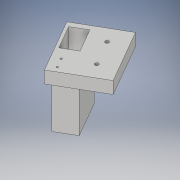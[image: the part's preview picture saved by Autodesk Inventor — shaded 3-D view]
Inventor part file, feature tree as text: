
AUTODESK INVENTOR PART (.ipt)
format: ipt  version: 2017 (Build 210142000, 142)  size: 245,248 bytes
history: native  units: in
note: dims shown in document units (in); Inventor stores cm internally (conversion verified against a paired STEP export)
features: extrude x7, sketch x7, projected_geometry x7, imported_body x1
ambient origin geometry x8: Origin, YZ Plane, XZ Plane, XY Plane, X Axis, Y Axis, Z Axis, Center Point
bodies: Solid1 (feature_tree)
feature tree (22):
  extrude  "Extrusion1"  Depth=0.3937in TaperAngle=0.0deg
  extrude  "Extrusion2"  Depth=0.3937in TaperAngle=0.0deg
  extrude  "Extrusion4"  Depth=0.3937in TaperAngle=0.0deg
  extrude  "Extrusion5"  Depth=0.3937in TaperAngle=0.0deg
  extrude  "Extrusion6"  Depth=0.188in
  extrude  "limit switch"  Depth=0.125in
  extrude  "Extrusion8"  Depth=0.3937in
  sketch  "Sketch1"  dims[d0=1.25in d1=0.3937in d2=0.0in]
  projected_geometry  "Projected Loop1"
  sketch  "Sketch2"  dims[d3=0.125in d4=0.3937in d5=0.0in]
  sketch  "Sketch4"  dims[d9=0.4331in d10=0.3937in d11=0.0in]
  projected_geometry  "Projected Loop3"
  sketch  "Sketch5"  dims[d12=0.3937in d13=0.3937in d14=0.0in]
  projected_geometry  "Projected Loop4"
  sketch  "Sketch6"  dims[d15=0.765in d16=0.188in]
  projected_geometry  "Projected Loop5"
  sketch  "Sketch7"  dims[d17=0.5in d18=0.125in]
  projected_geometry  "Projected Loop6"
  sketch  "Sketch10"  dims[d19=0.3937in d20=0.0in d21=0.276in d22=0.2in d23=0.575in d24=0.063in d25=0.3937in d26=0.0in d27=0.1181in d28=0.1181in d29=2.0in d30=0.0in]
  projected_geometry  "Projected Loop8"
  projected_geometry  "Projected Loop9"
  imported_body  "Base1"
